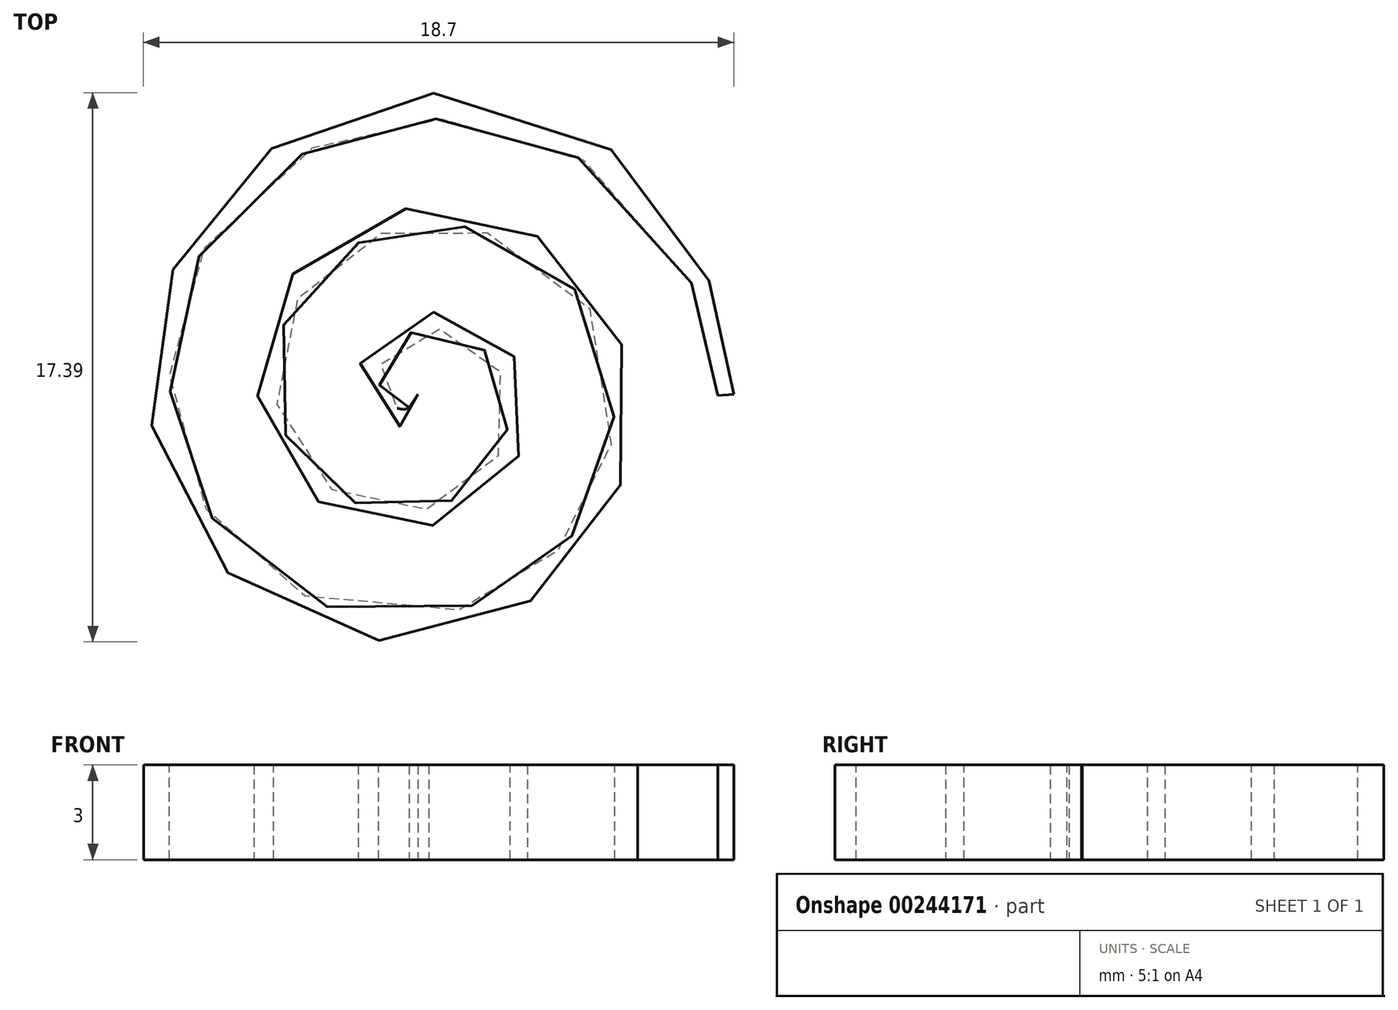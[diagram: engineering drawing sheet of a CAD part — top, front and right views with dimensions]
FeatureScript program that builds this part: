
annotation { "Feature Type Name" : "Feature", "Feature Type Description" : "" }
export const myFeature = defineFeature(function(context is Context, id is Id, definition is map)
    precondition{}
    {
        {
            var Q0;
            Q0=qCreatedBy(makeId("Top.planeOp"),FACE);
            var sketch = newSketch(context, id + "F0", { "sketchPlane" : qUnion([Q0])});
            skFitSpline(sketch, "E0", {"points": [v(10.28, 0.41) * mm, v(10.2, 1.9) * mm, v(9.79, 3.34) * mm, v(7.91, 6.78) * mm, v(5.9, 8.42) * mm, v(1.4, 9.87) * mm, v(-1.07, 9.69) * mm, v(-5.15, 7.73) * mm, v(-6.75, 5.97) * mm, v(-8.29, 1.93) * mm, v(-8.23, -0.34) * mm, v(-6.64, -4.14) * mm, v(-5.11, -5.67) * mm, v(-1.52, -7.25) * mm, v(0.52, -7.3) * mm, v(4.02, -6.03) * mm, v(5.46, -4.73) * mm, v(7.03, -1.58) * mm, v(7.16, 0.24) * mm, v(6.19, 3.41) * mm, v(5.1, 4.74) * mm, v(2.37, 6.26) * mm, v(0.77, 6.45) * mm, v(-2.05, 5.72) * mm, v(-3.25, 4.81) * mm, v(-4.68, 2.5) * mm, v(-4.9, 1.13) * mm, v(-4.37, -1.33) * mm, v(-3.64, -2.39) * mm, v(-1.72, -3.68) * mm, v(-0.56, -3.9) * mm, v(1.51, -3.54) * mm, v(2.42, -2.95) * mm, v(3.53, -1.4) * mm, v(3.74, -0.46) * mm, v(3.5, 1.23) * mm, v(3.04, 1.96) * mm, v(1.83, 2.86) * mm, v(1.1, 3.04) * mm, v(-0.2, 2.85) * mm, v(-0.75, 2.5) * mm, v(-1.53, 1.44) * mm, v(-1.55, 0.67) * mm, v(-1, -0.36) * mm, v(-0.48, -0.6) * mm, v(0.31, -0.5) * mm, v(0.57, -0.2) * mm, v(0.59, 0.26) * mm, v(0.44, 0.41) * mm, v(0.28, 0.41) * mm]});
            skFitSpline(sketch, "E1", {"points": [v(9.78, 0.39) * mm, v(9.74, 1.09) * mm, v(9.63, 1.78) * mm, v(9.2, 3.33) * mm, v(8.82, 4.16) * mm, v(7.4, 6.37) * mm, v(6.07, 7.53) * mm, v(3.74, 8.64) * mm, v(2.87, 8.9) * mm, v(1.1, 9.13) * mm, v(0.22, 9.11) * mm, v(-1.68, 8.8) * mm, v(-2.67, 8.43) * mm, v(-4.43, 7.38) * mm, v(-5.2, 6.7) * mm, v(-6.44, 5.13) * mm, v(-6.9, 4.26) * mm, v(-7.49, 2.42) * mm, v(-7.6, 1.46) * mm, v(-7.5, -0.4) * mm, v(-7.3, -1.3) * mm, v(-6.58, -2.95) * mm, v(-6.08, -3.7) * mm, v(-4.87, -4.97) * mm, v(-4.17, -5.49) * mm, v(-2.09, -6.52) * mm, v(-0.58, -6.73) * mm, v(1.5, -6.42) * mm, v(2.15, -6.21) * mm, v(3.35, -5.63) * mm, v(3.9, -5.25) * mm, v(4.97, -4.26) * mm, v(5.46, -3.61) * mm, v(6.16, -2.21) * mm, v(6.36, -1.45) * mm, v(6.5, 0.06) * mm, v(6.44, 0.82) * mm, v(5.9, 2.73) * mm, v(5.19, 3.8) * mm, v(3.76, 4.94) * mm, v(3.2, 5.25) * mm, v(2.03, 5.66) * mm, v(1.42, 5.76) * mm, v(0.24, 5.77) * mm, v(-0.33, 5.68) * mm, v(-1.39, 5.33) * mm, v(-1.88, 5.06) * mm, v(-2.83, 4.34) * mm, v(-3.27, 3.86) * mm, v(-3.9, 2.79) * mm, v(-4.1, 2.2) * mm, v(-4.28, 1) * mm, v(-4.25, 0.38) * mm, v(-3.95, -0.76) * mm, v(-3.69, -1.28) * mm, v(-3.05, -2.1) * mm, v(-2.7, -2.43) * mm, v(-1.94, -2.91) * mm, v(-1.52, -3.09) * mm, v(-0.58, -3.3) * mm, v(-0.06, -3.31) * mm, v(0.9, -3.14) * mm, v(1.35, -2.95) * mm, v(2.07, -2.46) * mm, v(2.35, -2.19) * mm, v(2.8, -1.57) * mm, v(2.95, -1.24) * mm, v(3.16, -0.48) * mm, v(3.18, -0.05) * mm, v(3.06, 0.73) * mm, v(2.91, 1.09) * mm, v(2.54, 1.65) * mm, v(2.33, 1.87) * mm, v(1.88, 2.2) * mm, v(1.63, 2.32) * mm, v(1.1, 2.46) * mm, v(0.83, 2.48) * mm, v(0.2, 2.42) * mm, v(-0.15, 2.26) * mm, v(-0.58, 1.9) * mm, v(-0.7, 1.75) * mm, v(-0.88, 1.42) * mm, v(-0.93, 1.25) * mm, v(-0.97, 0.9) * mm, v(-0.95, 0.72) * mm, v(-0.88, 0.45) * mm, v(-0.82, 0.36) * mm, v(-0.7, 0.19) * mm, v(-0.62, 0.12) * mm, v(-0.46, 0.01) * mm, v(-0.36, -0.03) * mm, v(-0.2, -0.06) * mm, v(-0.13, -0.05) * mm, v(-0.05, -0.03) * mm, v(-0.02, -0.01) * mm, v(0, 0) * mm]});
            skLineSegment(sketch, "E2", {"start": v(9.78, 0.39) * mm, "end": v(10.28, 0.41) * mm});
            skLineSegment(sketch, "E3", {"start": v(0, 0) * mm, "end": v(0.28, 0.41) * mm});
            skSolve(sketch);
        }
        {
            var Q0;
            Q0 = qSketchRegion(id + "F0", true);
            extrude(context, id + "F1", {"entities" : qUnion([Q0]), "depth" : 3 * mm});
        }
    });
